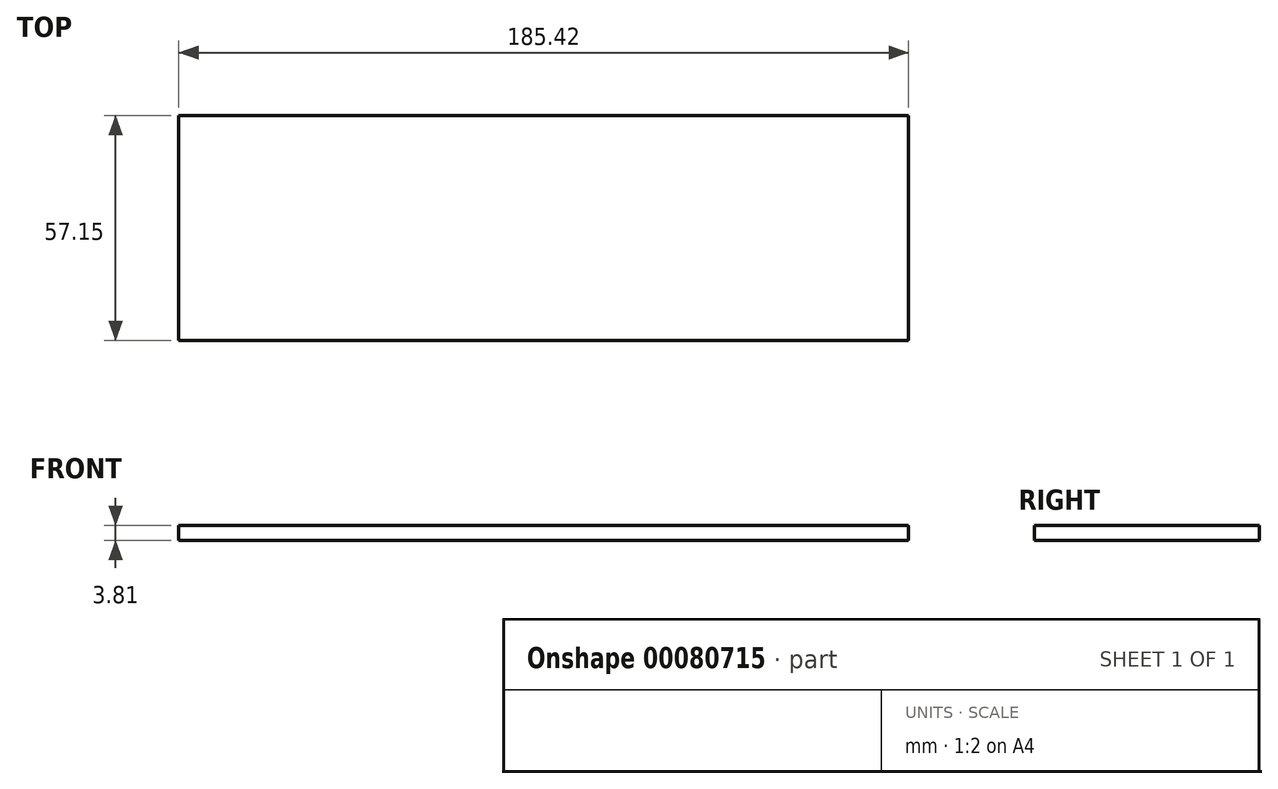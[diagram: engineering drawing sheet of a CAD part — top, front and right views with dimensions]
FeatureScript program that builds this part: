
annotation { "Feature Type Name" : "Feature", "Feature Type Description" : "" }
export const myFeature = defineFeature(function(context is Context, id is Id, definition is map)
    precondition{}
    {
        {
            var Q0;
            Q0=qCreatedBy(makeId("Top.planeOp"),FACE);
            var sketch = newSketch(context, id + "F0", { "sketchPlane" : qUnion([Q0])});
            skLineSegment(sketch, "E0.bottom", {"start": v(-50.27, 54.86) * mm, "end": v(135.15, 54.86) * mm});
            skLineSegment(sketch, "E0.top", {"start": v(-50.27, -2.29) * mm, "end": v(135.15, -2.29) * mm});
            skLineSegment(sketch, "E0.left", {"start": v(-50.27, 54.86) * mm, "end": v(-50.27, -2.29) * mm});
            skLineSegment(sketch, "E0.right", {"start": v(135.15, 54.86) * mm, "end": v(135.15, -2.29) * mm});
            skSolve(sketch);
        }
        {
            var Q0;
            Q0=makeQuery(id+"F0.imprint","IMPRINT",FACE,{"disambiguationData":[TD([[makeQuery(id+"F0.imprint","IMPRINT",EDGE,{"derivedFrom":sQuery(id+"F0.wireOp",EDGE,"E0.bottom")}),-1.0]])]});
            extrude(context, id + "F1", {"entities" : qUnion([Q0]), "depth" : 3.8 * mm});
        }
    });
